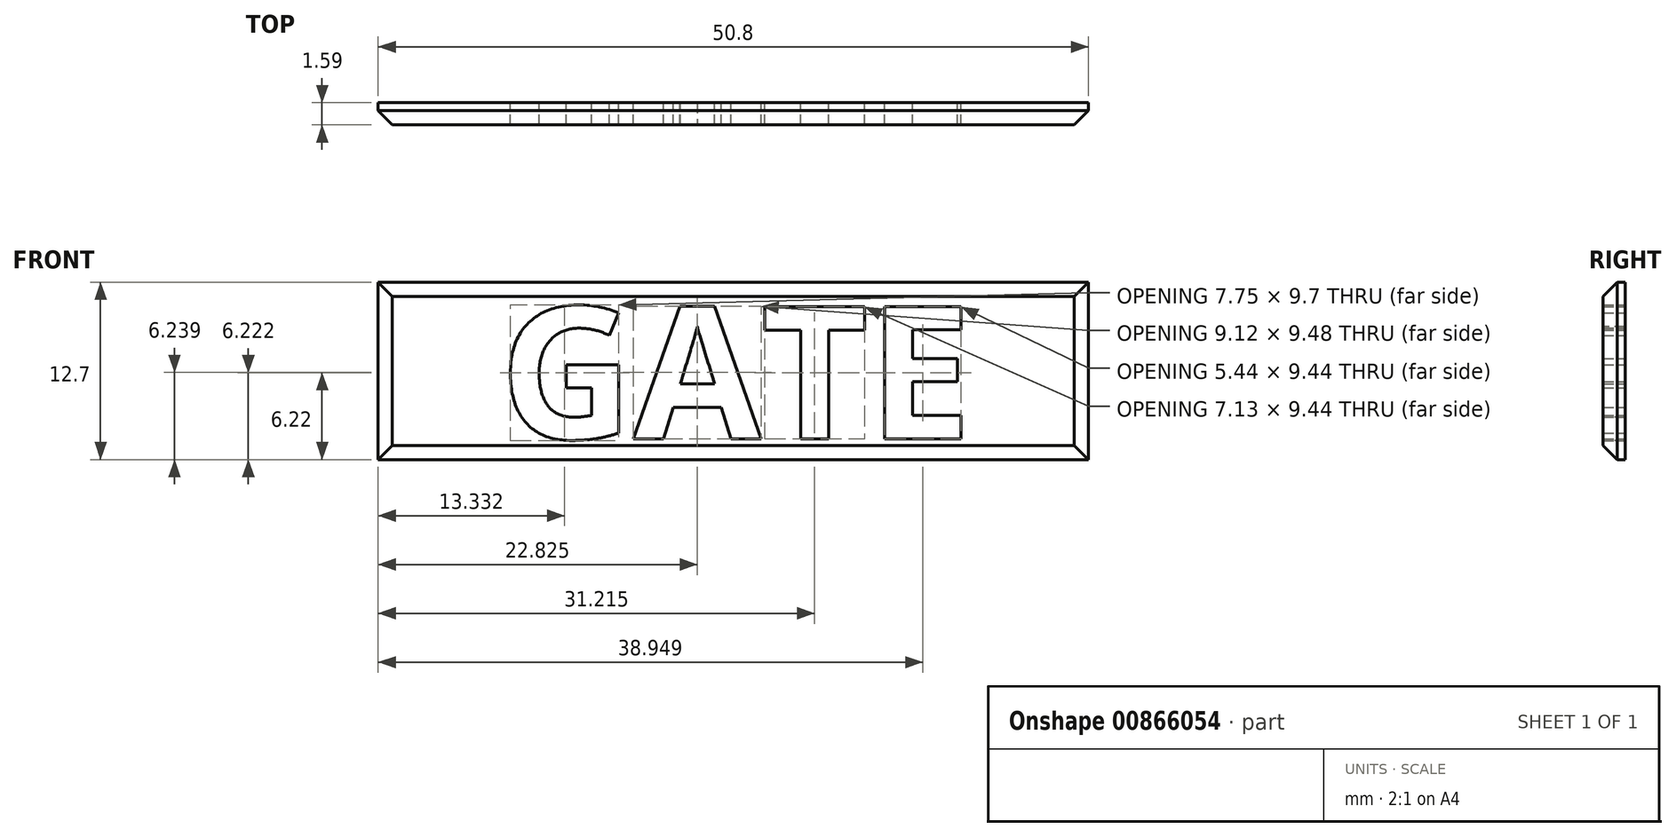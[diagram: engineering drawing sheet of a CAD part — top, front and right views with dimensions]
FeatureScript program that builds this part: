
annotation { "Feature Type Name" : "Feature", "Feature Type Description" : "" }
export const myFeature = defineFeature(function(context is Context, id is Id, definition is map)
    precondition{}
    {
        {
            var Q0;
            Q0=qCreatedBy(makeId("Front.planeOp"),FACE);
            var sketch = newSketch(context, id + "F0", { "sketchPlane" : qUnion([Q0])});
            skLineSegment(sketch, "E0.bottom", {"start": v(-34.56, 16.68) * mm, "end": v(16.24, 16.68) * mm});
            skLineSegment(sketch, "E0.top", {"start": v(-34.56, 3.98) * mm, "end": v(16.24, 3.98) * mm});
            skLineSegment(sketch, "E0.left", {"start": v(-34.56, 16.68) * mm, "end": v(-34.56, 3.98) * mm});
            skLineSegment(sketch, "E0.right", {"start": v(16.24, 16.68) * mm, "end": v(16.24, 3.98) * mm});
            skText(sketch, "E1", { "text": "GATE", "fontName": "OpenSans-Bold.ttf"});
            const initialGuessF0  = {"E1": [-0.02587, 0.00548, 1, 0, 0.00952]};
            skSetInitialGuess(sketch, initialGuessF0);
            skSolve(sketch);
        }
        {
            var Q0;
            Q0=makeQuery(id+"F0.imprint","IMPRINT",FACE,{"disambiguationData":[TD([[makeQuery(id+"F0.imprint","IMPRINT",EDGE,{"derivedFrom":sQuery(id+"F0.wireOp",EDGE,"E0.bottom")}),-1.0]])]});
            var Q1;
            Q1=makeQuery(id+"F0.imprint","IMPRINT",FACE,{"disambiguationData":[TD([[makeQuery(id+"F0.imprint","IMPRINT",EDGE,{"derivedFrom":sQuery(id+"F0.wireOp",EDGE,"E1.sketch_text.stroke-66")}),1.0]])]});
            var Q2;
            Q2=makeQuery(id+"F0.imprint","IMPRINT",FACE,{"disambiguationData":[TD([[makeQuery(id+"F0.imprint","IMPRINT",EDGE,{"derivedFrom":sQuery(id+"F0.wireOp",EDGE,"E1.sketch_text.stroke-60")}),1.0]])]});
            var Q3;
            Q3=makeQuery(id+"F0.imprint","IMPRINT",FACE,{"disambiguationData":[TD([[makeQuery(id+"F0.imprint","IMPRINT",EDGE,{"derivedFrom":sQuery(id+"F0.wireOp",EDGE,"E1.sketch_text.stroke-27")}),1.0]])]});
            extrude(context, id + "F1", {"entities" : qUnion([Q0, Q1, Q2, Q3]), "depth" : 1.59 * mm, "offsetDistance" : 25.4 * mm});
        }
        {
            var Q0;
            Q0=makeQuery(id+"F1.opExtrude","CAP_EDGE",EDGE,{"disambiguationData":[OSD([sQuery(id+"F0.wireOp",EDGE,"E0.top")])],"isStart":false});
            var Q1;
            Q1=makeQuery(id+"F1.opExtrude","CAP_EDGE",EDGE,{"disambiguationData":[OSD([sQuery(id+"F0.wireOp",EDGE,"E0.left")])],"isStart":false});
            var Q2;
            Q2=makeQuery(id+"F1.opExtrude","CAP_EDGE",EDGE,{"disambiguationData":[OSD([sQuery(id+"F0.wireOp",EDGE,"E0.bottom")])],"isStart":false});
            var Q3;
            Q3=makeQuery(id+"F1.opExtrude","CAP_EDGE",EDGE,{"disambiguationData":[OSD([sQuery(id+"F0.wireOp",EDGE,"E0.right")])],"isStart":false});
            chamfer(context, id + "F2", {"entities" : qUnion([Q0, Q1, Q2, Q3]), "width" : 1.02 * mm, "tangentPropagation" : true});
        }
    });
